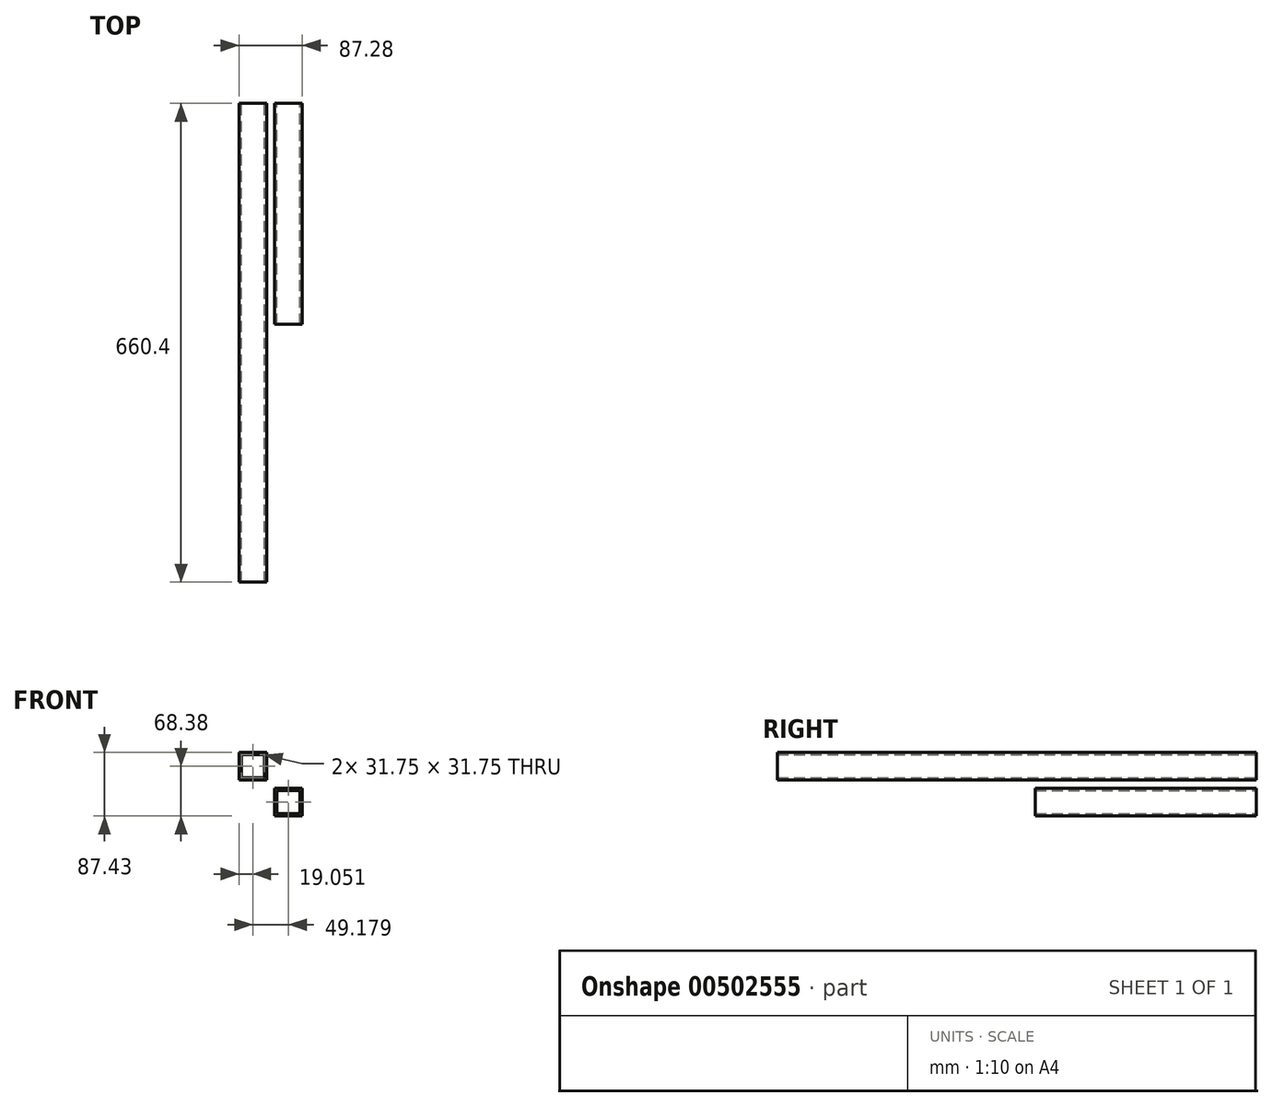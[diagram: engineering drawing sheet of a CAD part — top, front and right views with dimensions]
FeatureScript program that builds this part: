
annotation { "Feature Type Name" : "Feature", "Feature Type Description" : "" }
export const myFeature = defineFeature(function(context is Context, id is Id, definition is map)
    precondition{}
    {
        {
            var Q0;
            Q0=qCreatedBy(makeId("Front.planeOp"),FACE);
            var sketch = newSketch(context, id + "F0", { "sketchPlane" : qUnion([Q0])});
            skLineSegment(sketch, "E0.bottom", {"start": v(19.05, 19.05) * mm, "end": v(-19.05, 19.05) * mm});
            skLineSegment(sketch, "E0.top", {"start": v(19.05, -19.05) * mm, "end": v(-19.05, -19.05) * mm});
            skLineSegment(sketch, "E0.left", {"start": v(19.05, 19.05) * mm, "end": v(19.05, -19.05) * mm});
            skLineSegment(sketch, "E0.right", {"start": v(-19.05, 19.05) * mm, "end": v(-19.05, -19.05) * mm});
            skPoint(sketch, "E0.middle", {"position": v(0, 0) * mm});
            skLineSegment(sketch, "E1.bottom", {"start": v(15.88, 15.88) * mm, "end": v(-15.88, 15.88) * mm});
            skLineSegment(sketch, "E1.top", {"start": v(15.87, -15.88) * mm, "end": v(-15.88, -15.88) * mm});
            skLineSegment(sketch, "E1.left", {"start": v(15.88, 15.88) * mm, "end": v(15.88, -15.88) * mm});
            skLineSegment(sketch, "E1.right", {"start": v(-15.88, 15.88) * mm, "end": v(-15.88, -15.88) * mm});
            skSolve(sketch);
        }
        {
            var Q0;
            Q0=makeQuery(id+"F0.imprint","IMPRINT",FACE,{"disambiguationData":[TD([[makeQuery(id+"F0.imprint","IMPRINT",EDGE,{"derivedFrom":sQuery(id+"F0.wireOp",EDGE,"E0.bottom")}),1.0]])]});
            extrude(context, id + "F1", {"entities" : qUnion([Q0]), "depth" : 304.8 * mm, "offsetDistance" : 25.4 * mm});
        }
        {
            var Q0;
            Q0=qCreatedBy(makeId("Front.planeOp"),FACE);
            var sketch = newSketch(context, id + "F2", { "sketchPlane" : qUnion([Q0])});
            skLineSegment(sketch, "E2.bottom", {"start": v(-30.13, 68.38) * mm, "end": v(-68.23, 68.38) * mm});
            skLineSegment(sketch, "E2.top", {"start": v(-30.13, 30.28) * mm, "end": v(-68.23, 30.28) * mm});
            skLineSegment(sketch, "E2.left", {"start": v(-30.13, 68.38) * mm, "end": v(-30.13, 30.28) * mm});
            skLineSegment(sketch, "E2.right", {"start": v(-68.23, 68.38) * mm, "end": v(-68.23, 30.28) * mm});
            skPoint(sketch, "E2.middle", {"position": v(-49.18, 49.33) * mm});
            skLineSegment(sketch, "E3.bottom", {"start": v(-33.3, 65.2) * mm, "end": v(-65.05, 65.2) * mm});
            skLineSegment(sketch, "E3.top", {"start": v(-33.3, 33.45) * mm, "end": v(-65.05, 33.45) * mm});
            skLineSegment(sketch, "E3.left", {"start": v(-33.3, 65.2) * mm, "end": v(-33.3, 33.45) * mm});
            skLineSegment(sketch, "E3.right", {"start": v(-65.05, 65.2) * mm, "end": v(-65.05, 33.45) * mm});
            skSolve(sketch);
        }
        {
            var Q0;
            Q0=makeQuery(id+"F2.imprint","IMPRINT",FACE,{"disambiguationData":[TD([[makeQuery(id+"F2.imprint","IMPRINT",EDGE,{"derivedFrom":sQuery(id+"F2.wireOp",EDGE,"E2.bottom")}),1.0]])]});
            extrude(context, id + "F3", {"entities" : qUnion([Q0]), "depth" : 660.4 * mm, "offsetDistance" : 25.4 * mm});
        }
    });
